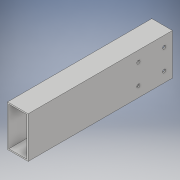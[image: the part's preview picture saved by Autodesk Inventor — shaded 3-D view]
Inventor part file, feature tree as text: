
AUTODESK INVENTOR PART (.ipt)
format: ipt  version: 2018 (Build 220112000, 112)  size: 114,176 bytes
history: native  units: in
note: dims shown in document units (in); Inventor stores cm internally (conversion verified against a paired STEP export)
features: extrude x2, sketch x2
ambient origin geometry x8: Origin, YZ Plane, XZ Plane, XY Plane, X Axis, Y Axis, Z Axis, Center Point
bodies: Solid1 (feature_tree)
feature tree (4):
  extrude  "Extrusion1"  Depth=2.0in
  extrude  "Extrusion2"  Depth=7.0in TaperAngle=0.0deg
  sketch  "Sketch1"  dims[d0=1.0in d1=2.0in]
  sketch  "Sketch2"  dims[d2=0.0625in d3=7.0in d4=0.0in d5=0.5in d6=0.402in d7=1.0in d9=1.25in d10=0.159in d11=7.0in d12=0.0in]
